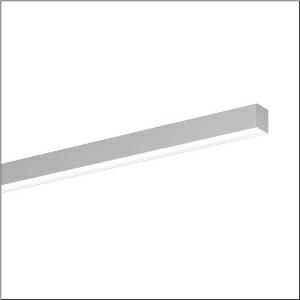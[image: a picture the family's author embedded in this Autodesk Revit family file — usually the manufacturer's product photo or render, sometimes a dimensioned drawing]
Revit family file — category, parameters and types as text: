
# Revit family: silica_r__21_51mx20tat2s_7558
name_source: partatom
category: Lighting Fixtures
units: mm (PartAtom-declared; Revit-internal decimal feet)

## family parameters
Cut with Voids When Loaded = No
Host = Face
Light Source = No
Part Type = Normal
Room Calculation Point = No
Round Connector Dimension = Use Diameter
Shared = No

## types (1)
- --- (1 x LED, 2400 lm, 20.5 W, 6500K)
    Apparent Load = 21 VA
    CIE Flux Codes = 48 79 96 100 100
    Color Rendering = 80
    Color Temperature = 6500K
    Default Elevation = 1800 mm
    Description = Silica® 21, office luminaire, primary optical cover: cover, of PMMA, opal, light emission: direct distribution, primary light characteristic: symmetric, installation type: surface-mounted, LED, rated luminous flux: 2.400lm, luminous efficacy: 112lm/W, light colour: 8tw, colour temperature: 2700..6500K, control gear: DALI DT8, with terminal, 3+2-pole, max. 2.5mm², mains connection: 220..240V, AC, 50/60Hz, rated input power: 21.5W, luminaire housing, of aluminium, metallic grey (RAL 9006), length: 1.204mm, width: 53mm, height: 53mm, protection rating (complete): IP20, insulation class (complete): insulation class I (protective earthing), certification: CE, permissible operating ambient temperature: 0..+35°C, standard: EN 50419, packaging unit: 1 piece
    Height = 53 mm
    Lamp = 1 x LED
    Lamp Light Flux = 2400 lm
    Lamp Power = 20.5 W
    Lamp count = 1
    Length = 1204 mm
    Luminous efficacy = 117 lm/W
    Manufacturer = Siteco
    ModVariant = No
    Model = 51MX20TAT2S
    Mounting Place = Ceiling
    Mounting Type = Surface mounted
    Number of Poles = 1
    OnlyDefault = Yes
    Power Factor = 1
    Product Name = Silica® 21
    Product group = office luminaire | ceiling mounted
    ProductGroupID = 303
    Protection Class = Protection class I
    Protection Degree = IP 20
    RLX_Detail_Level = 1
    RLX_Emergency_Light_Flux = 0 lm
    RLX_Emergency_Type = 0
    RLX_Emergency_Type_DB = No
    RlxData = <blob elided: 23141 chars, md5=e1c9c40a>
    Socket = socket
    Standby Power = 0 W
    System Light Flux = 2400 lm
    System Power = 21 W
    Type Comments = individual setting
    Type Image = l_1335933.jpg
    URL = http://relux.com
    VarID = @adj_161153
    Voltage = 0 V
    Weight = 0.00 kg
    Width = 53 mm

## geometry (parser evidence)
native form markers: Blend x4, Sweep x11
no freeform markers — native parametric forms only
